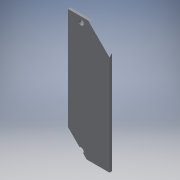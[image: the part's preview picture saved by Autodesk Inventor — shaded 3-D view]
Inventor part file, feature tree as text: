
AUTODESK INVENTOR PART (.ipt)
format: ipt  version: 2016 (Build 200138000, 138)  size: 104,960 bytes
history: native  units: mm
features: extrude x2, sketch x2, other x1
ambient origin geometry x8: Origin, YZ Plane, XZ Plane, XY Plane, X Axis, Y Axis, Z Axis, Center Point
bodies: Body1 (feature_tree)
feature tree (5):
  other  "ソリッド1"
  extrude  "押し出し1"  Depth=1.0mm TaperAngle=0.0deg
  extrude  "押し出し2"  Depth=2.0mm
  sketch  "スケッチ1"
  sketch  "スケッチ2"
